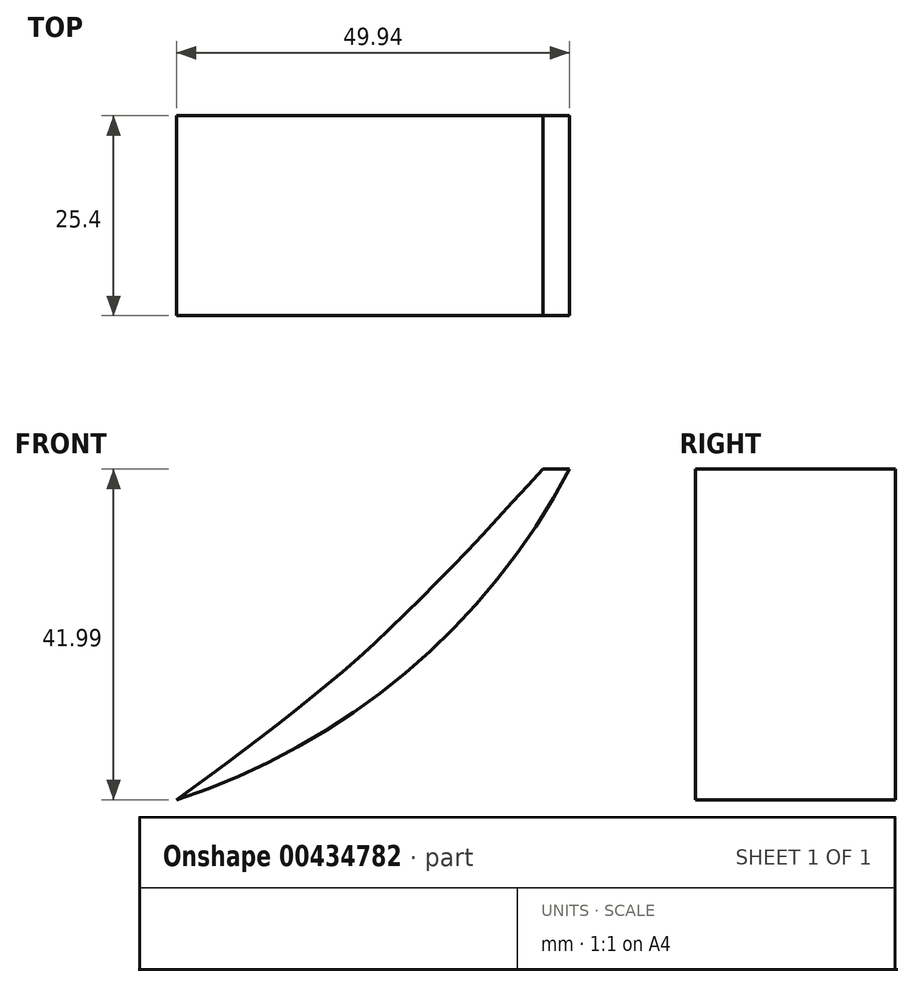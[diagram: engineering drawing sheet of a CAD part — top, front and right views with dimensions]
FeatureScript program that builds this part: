
annotation { "Feature Type Name" : "Feature", "Feature Type Description" : "" }
export const myFeature = defineFeature(function(context is Context, id is Id, definition is map)
    precondition{}
    {
        {
            var Q0;
            Q0=qCreatedBy(makeId("Front.planeOp"),FACE);
            var sketch = newSketch(context, id + "F0", { "sketchPlane" : qUnion([Q0])});
            skArc(sketch, "E0", {"start": v(0, 0) * mm, "mid": v(29.08, 16.1) * mm, "end": v(49.94, 42) * mm});
            skLineSegment(sketch, "E1", {"start": v(46.53, 42) * mm, "end": v(49.94, 42) * mm});
            skFitSpline(sketch, "E2", {"points": [v(46.53, 42) * mm, v(23.55, 18.44) * mm, v(0, 0) * mm], "startDerivative": vector(-44.03, -48.1) * mm, "endDerivative": vector(-49.07, -35.78) * mm});
            skSolve(sketch);
        }
        {
            var Q0;
            Q0=makeQuery(id+"F0.imprint","IMPRINT",FACE,{"disambiguationData":[TD([[makeQuery(id+"F0.imprint","IMPRINT",EDGE,{"derivedFrom":sQuery(id+"F0.wireOp",EDGE,"E0")}),1.0]])]});
            extrude(context, id + "F1", {"entities" : qUnion([Q0]), "oppositeDirection" : true, "depth" : 25.4 * mm});
        }
    });
